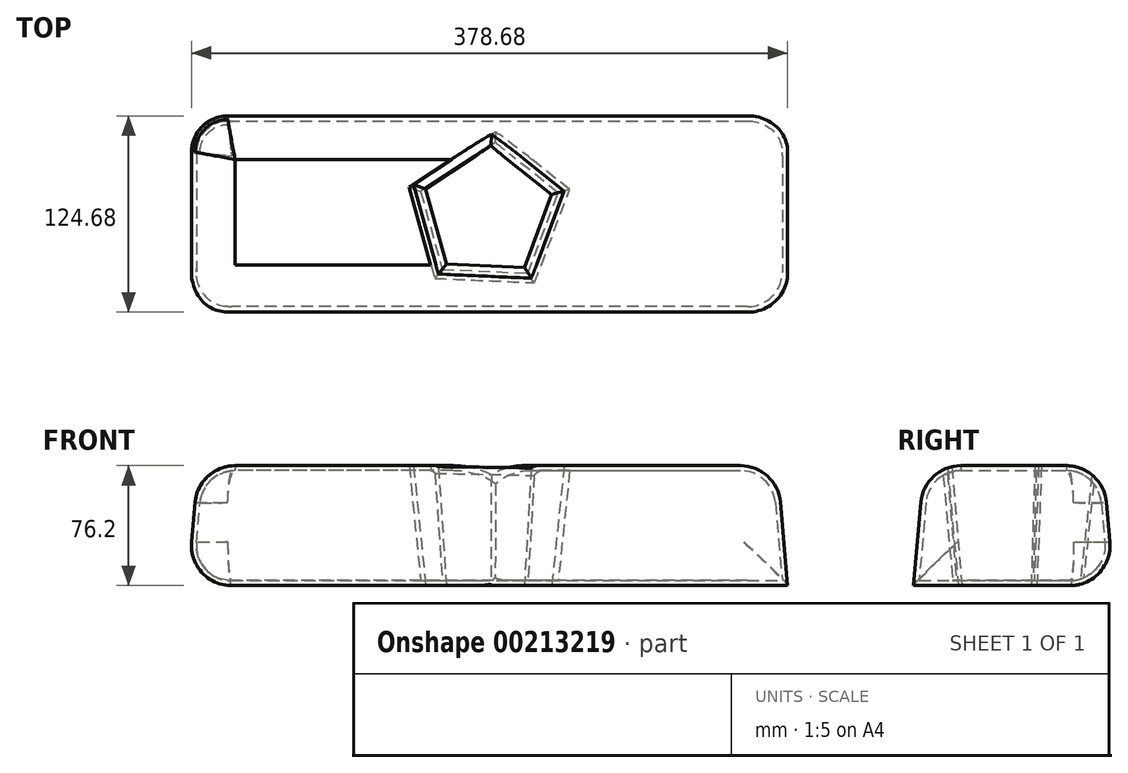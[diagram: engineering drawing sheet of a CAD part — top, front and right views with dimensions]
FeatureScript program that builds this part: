
annotation { "Feature Type Name" : "Feature", "Feature Type Description" : "" }
export const myFeature = defineFeature(function(context is Context, id is Id, definition is map)
    precondition{}
    {
        {
            var Q0;
            Q0=qCreatedBy(makeId("Top.planeOp"),FACE);
            var sketch = newSketch(context, id + "F0", { "sketchPlane" : qUnion([Q0])});
            skLineSegment(sketch, "E0.bottom", {"start": v(190.5, -63.5) * mm, "end": v(-190.5, -63.5) * mm});
            skLineSegment(sketch, "E0.top", {"start": v(190.5, 63.5) * mm, "end": v(-165.1, 63.5) * mm});
            skLineSegment(sketch, "E0.left", {"start": v(190.5, -63.5) * mm, "end": v(190.5, 63.5) * mm});
            skLineSegment(sketch, "E0.right", {"start": v(-190.5, -63.5) * mm, "end": v(-190.5, 38.1) * mm});
            skPoint(sketch, "E0.middle", {"position": v(0, 0) * mm});
            skPoint(sketch, "E1.visualSharp", {"position": v(-190.5, 63.5) * mm});
            skArc(sketch, "E1.filletArc", {"start": v(-165.1, 63.5) * mm, "mid": v(-183.06, 56.06) * mm, "end": v(-190.5, 38.1) * mm});
            skCircle(sketch, "E2.cCircle", {"center": v(0, 0) * mm, "radius": 34.08 * mm, "construction": true});
            skLineSegment(sketch, "E2.0", {"start": v(40.6, 11.19) * mm, "end": v(23.19, -35.17) * mm});
            skLineSegment(sketch, "E2.1", {"start": v(23.19, -35.17) * mm, "end": v(-26.28, -32.92) * mm});
            skLineSegment(sketch, "E2.2", {"start": v(-26.28, -32.92) * mm, "end": v(-39.43, 14.82) * mm});
            skLineSegment(sketch, "E2.3", {"start": v(-39.43, 14.82) * mm, "end": v(1.9, 42.08) * mm});
            skLineSegment(sketch, "E2.4", {"start": v(1.9, 42.08) * mm, "end": v(40.6, 11.19) * mm});
            skPoint(sketch, "E2.0.midPoint", {"position": v(31.9, -11.99) * mm});
            skSolve(sketch);
        }
        {
            var Q0;
            Q0=makeQuery(id+"F0.imprint","IMPRINT",FACE,{"disambiguationData":[TD([[makeQuery(id+"F0.imprint","IMPRINT",EDGE,{"derivedFrom":sQuery(id+"F0.wireOp",EDGE,"E0.bottom")}),-1.0]])]});
            extrude(context, id + "F1", {"entities" : qUnion([Q0]), "depth" : 76.2 * mm, "offsetDistance" : 25.4 * mm, "hasDraft" : true, "draftAngle" : 5 * degree, "draftPullDirection" : true});
        }
        {
            var Q0;
            Q0=makeQuery(id+"F1.opExtrude","CAP_EDGE",EDGE,{"disambiguationData":[OSD([sQuery(id+"F0.wireOp",EDGE,"E0.right")])],"isStart":false});
            var Q1;
            Q1=makeQuery(id+"F1.opExtrude","CAP_EDGE",EDGE,{"disambiguationData":[OSD([sQuery(id+"F0.wireOp",EDGE,"E0.bottom")])],"isStart":false});
            var Q2;
            Q2=makeQuery(id+"F1.opExtrude","CAP_EDGE",EDGE,{"disambiguationData":[OSD([sQuery(id+"F0.wireOp",EDGE,"E0.left")])],"isStart":false});
            var Q3;
            Q3=makeQuery(id+"F1.opExtrude","CAP_EDGE",EDGE,{"disambiguationData":[OSD([sQuery(id+"F0.wireOp",EDGE,"E0.top")])],"isStart":false});
            var Q4;
            Q4=makeQuery(id+"F1.opExtrude","SWEPT_EDGE",EDGE,{"disambiguationData":[OSD([sQuery(id+"F0.wireOp",EDGE,"E0.bottom"),sQuery(id+"F0.wireOp",EDGE,"E0.right")])]});
            var Q5;
            Q5=makeQuery(id+"F1.opExtrude","SWEPT_FACE",FACE,{"disambiguationData":[OSD([sQuery(id+"F0.wireOp",EDGE,"E0.top")])]});
            var Q6;
            Q6=makeQuery(id+"F1.opExtrude","SWEPT_EDGE",EDGE,{"disambiguationData":[OSD([sQuery(id+"F0.wireOp",EDGE,"E0.bottom"),sQuery(id+"F0.wireOp",EDGE,"E0.left")])]});
            fillet(context, id + "F2", {"entities" : qUnion([Q0, Q1, Q2, Q3, Q4, Q5, Q6]), "radius" : 25.4 * mm, "tangentPropagation" : true, "allowEdgeOverflow" : false});
        }
        {
            var Q0;
            Q0=makeQuery(id+"F2.opFillet","SPLIT",FACE,{"disambiguationData":[OD(1.0)],"derivedFrom":makeQuery(id+"F1.opExtrude","CAP_FACE",FACE,{"disambiguationData":[OSD([sQuery(id+"F0.wireOp",EDGE,"E0.bottom"),sQuery(id+"F0.wireOp",EDGE,"E0.top"),sQuery(id+"F0.wireOp",EDGE,"E0.left"),sQuery(id+"F0.wireOp",EDGE,"E0.right"),sQuery(id+"F0.wireOp",EDGE,"E1.filletArc"),sQuery(id+"F0.wireOp",EDGE,"E2.0"),sQuery(id+"F0.wireOp",EDGE,"E2.1"),sQuery(id+"F0.wireOp",EDGE,"E2.2"),sQuery(id+"F0.wireOp",EDGE,"E2.3"),sQuery(id+"F0.wireOp",EDGE,"E2.4")])],"isStart":false})});
            shell(context, id + "F3", {"entities" : qUnion([Q0]), "thickness" : 3.17 * mm});
        }
    });
